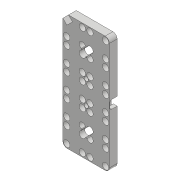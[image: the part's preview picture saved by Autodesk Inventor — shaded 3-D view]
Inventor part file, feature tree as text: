
AUTODESK INVENTOR PART (.ipt)
format: ipt  version: 2018 (Build 220112000, 112)  size: 1,002,496 bytes
history: native  units: mm
features: projected_geometry x15, extrude x13, sketch x12, pattern_linear x6, fillet x6
ambient origin geometry x8: Origin, YZ Plane, XZ Plane, XY Plane, X Axis, Y Axis, Z Axis, Center Point
bodies: Solid1 (feature_tree)
feature tree (52):
  extrude  "Extrusion1"  Depth=44.0mm
  extrude  "Extrusion2"  Depth=22.0mm
  extrude  "Extrusion3"  Depth=22.0mm
  pattern_linear  "Rectangular Pattern1"  Count1=5 Spacing1=22.0mm
  extrude  "Extrusion4"  Depth=10.0mm
  pattern_linear  "Rectangular Pattern2"  Spacing1=5.0mm  [1 undecoded]
  extrude  "Extrusion5"  Depth=5.0mm
  pattern_linear  "Rectangular Pattern3"  Spacing1=2.0mm  [1 undecoded]
  fillet  "Fillet1"  Radius=50.0mm
  extrude  "Extrusion6"  Depth=2.0mm TaperAngle=0.0deg
  extrude  "Extrusion9"  Depth=22.0mm
  pattern_linear  "Rectangular Pattern4"  Spacing1=1.0mm  [1 undecoded]
  extrude  "Extrusion7"  Depth=12.0mm
  pattern_linear  "Rectangular Pattern5"  Spacing1=6.7mm  [1 undecoded]
  pattern_linear  "Rectangular Pattern6"  Count1=2 Spacing1=66.0mm
  fillet  "Fillet2"  Radius=4.0mm
  fillet  "Fillet3"  Radius=2.0mm
  fillet  "Fillet4"  Radius=22.0mm
  extrude  "Extrusion8"  Depth=4.0mm
  fillet  "Fillet5"  Radius=0.5mm
  extrude  "Extrusion10"  Depth=1.0mm
  extrude  "Extrusion11"  Depth=2.5mm
  fillet  "Fillet6"  Radius=3.0mm
  extrude  "Extrusion12"  Depth=0.5mm
  extrude  "Extrusion13"  Depth=2.0mm
  sketch  "Sketch1"  dims[d0=110.0mm d1=44.0mm]
  sketch  "Sketch2"  dims[d2=7.3mm d3=0.0mm d4=22.0mm]
  projected_geometry  "Projected Loop1"
  sketch  "Sketch3"  dims[d5=22.0mm d6=14.75mm]
  projected_geometry  "Projected Loop2"
  projected_geometry  "Projected Loop3"
  projected_geometry  "Projected Loop4"
  projected_geometry  "Projected Loop5"
  sketch  "Sketch4"  dims[d7=7.5mm]
  projected_geometry  "Projected Loop6"
  sketch  "Sketch5"  dims[d8=7.0mm d9=0.0mm]
  projected_geometry  "Projected Loop7"
  projected_geometry  "Projected Loop8"
  sketch  "Sketch7"  dims[d10=6.7mm d11=0.0mm]
  projected_geometry  "Projected Loop9"
  sketch  "Sketch8"  dims[d12=6.0mm]
  projected_geometry  "Projected Loop10"
  sketch  "Sketch9"  dims[d13=6.0mm]
  sketch  "Sketch10"  dims[d14=6.0mm]
  sketch  "Sketch11"  dims[d15=6.0mm d16=50.0mm d18=22.0mm]
  projected_geometry  "Projected Loop11"
  projected_geometry  "Projected Loop12"
  projected_geometry  "Projected Loop13"
  sketch  "Sketch12"  dims[d19=20.0mm d21=22.0mm d22=10.0mm]
  projected_geometry  "Projected Loop14"
  sketch  "Sketch13"  dims[d23=5.0mm d24=5.0mm d25=5.0mm d26=2.0mm d27=0.0mm d28=50.0mm d30=22.0mm d31=2.0mm d32=0.0mm d33=20.0mm d35=22.0mm d36=1.0mm d37=8.5mm d38=6.7mm d39=0.0mm d40=20.0mm d42=66.0mm d43=4.0mm d44=2.0mm d45=0.0mm d46=20.0mm d48=22.0mm d49=4.0mm d50=0.5mm d51=1.0mm d52=2.5mm d53=3.0mm d54=0.0mm d55=0.5mm d56=2.0mm d57=2.0mm d58=2.0mm d59=2.0mm d60=2.0mm d61=2.0mm d62=2.0mm d63=2.0mm d64=10.0mm d65=0.0mm d66=40.0mm d68=22.0mm d69=8.0mm d70=10.0mm d71=0.0mm d72=10.0mm d73=0.0mm d74=2.0mm d75=45.0deg d76=18.0mm d77=7.5mm d78=10.0mm d79=0.0mm d80=4.0mm d81=12.0mm d82=0.0mm d83=0.0mm]
  projected_geometry  "Projected Loop15"
note: 4 required parameter values undecoded (feature->parameter linkage not recoverable at this tier; creation-order binding heuristic only, values carry confidence <= 0.55)
